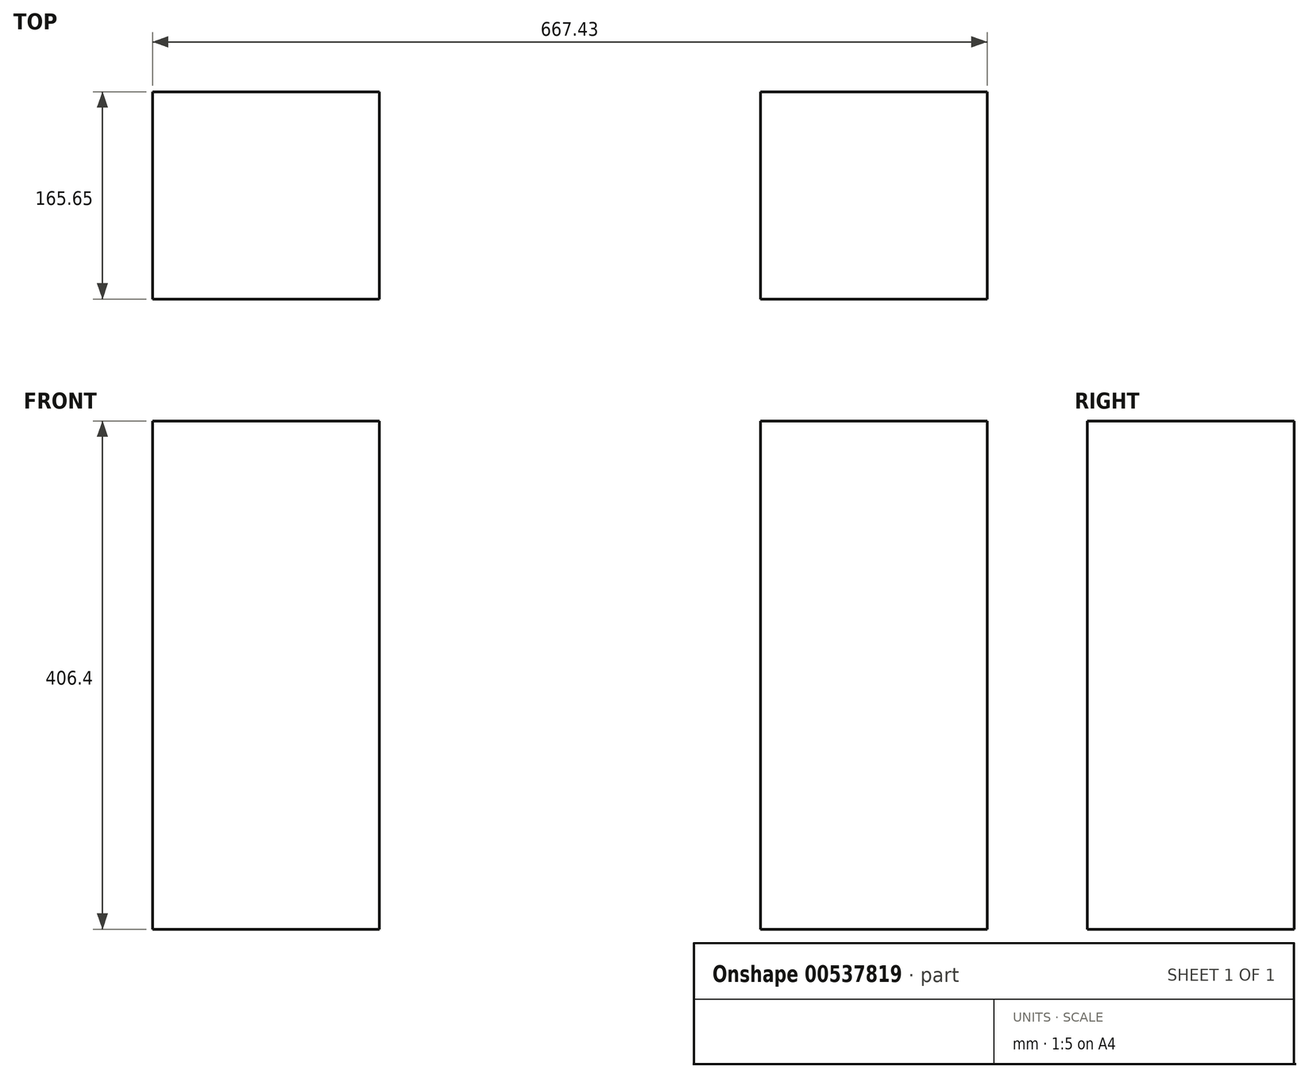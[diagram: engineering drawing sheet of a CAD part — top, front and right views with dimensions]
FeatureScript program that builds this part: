
annotation { "Feature Type Name" : "Feature", "Feature Type Description" : "" }
export const myFeature = defineFeature(function(context is Context, id is Id, definition is map)
    precondition{}
    {
        {
            var Q0;
            Q0=qCreatedBy(makeId("Top.planeOp"),FACE);
            var sketch = newSketch(context, id + "F0", { "sketchPlane" : qUnion([Q0])});
            skLineSegment(sketch, "E0", {"start": v(0, 0) * mm, "end": v(0, 165.65) * mm});
            skLineSegment(sketch, "E1", {"start": v(0, 165.65) * mm, "end": v(181.32, 165.65) * mm});
            skLineSegment(sketch, "E2", {"start": v(181.32, 165.65) * mm, "end": v(181.32, 0) * mm});
            skLineSegment(sketch, "E3", {"start": v(181.32, 0) * mm, "end": v(0, 0) * mm});
            skLineSegment(sketch, "E4", {"start": v(181.32, 0) * mm, "end": v(486.12, 0) * mm});
            skLineSegment(sketch, "E5", {"start": v(333.72, 0) * mm, "end": v(333.72, 165.65) * mm});
            skLineSegment(sketch, "E6.MirrorCS", {"start": v(486.12, 165.65) * mm, "end": v(486.12, 0) * mm});
            skLineSegment(sketch, "E7.MirrorCS", {"start": v(667.43, 165.65) * mm, "end": v(486.12, 165.65) * mm});
            skLineSegment(sketch, "E8.MirrorCS", {"start": v(667.43, 0) * mm, "end": v(667.43, 165.65) * mm});
            skLineSegment(sketch, "E9.MirrorCS", {"start": v(486.12, 0) * mm, "end": v(667.43, 0) * mm});
            skSolve(sketch);
        }
        {
            var Q0;
            Q0 = qSketchRegion(id + "F0", true);
            extrude(context, id + "F1", {"entities" : qUnion([Q0]), "depth" : 406.4 * mm, "offsetDistance" : 25.4 * mm});
        }
    });
